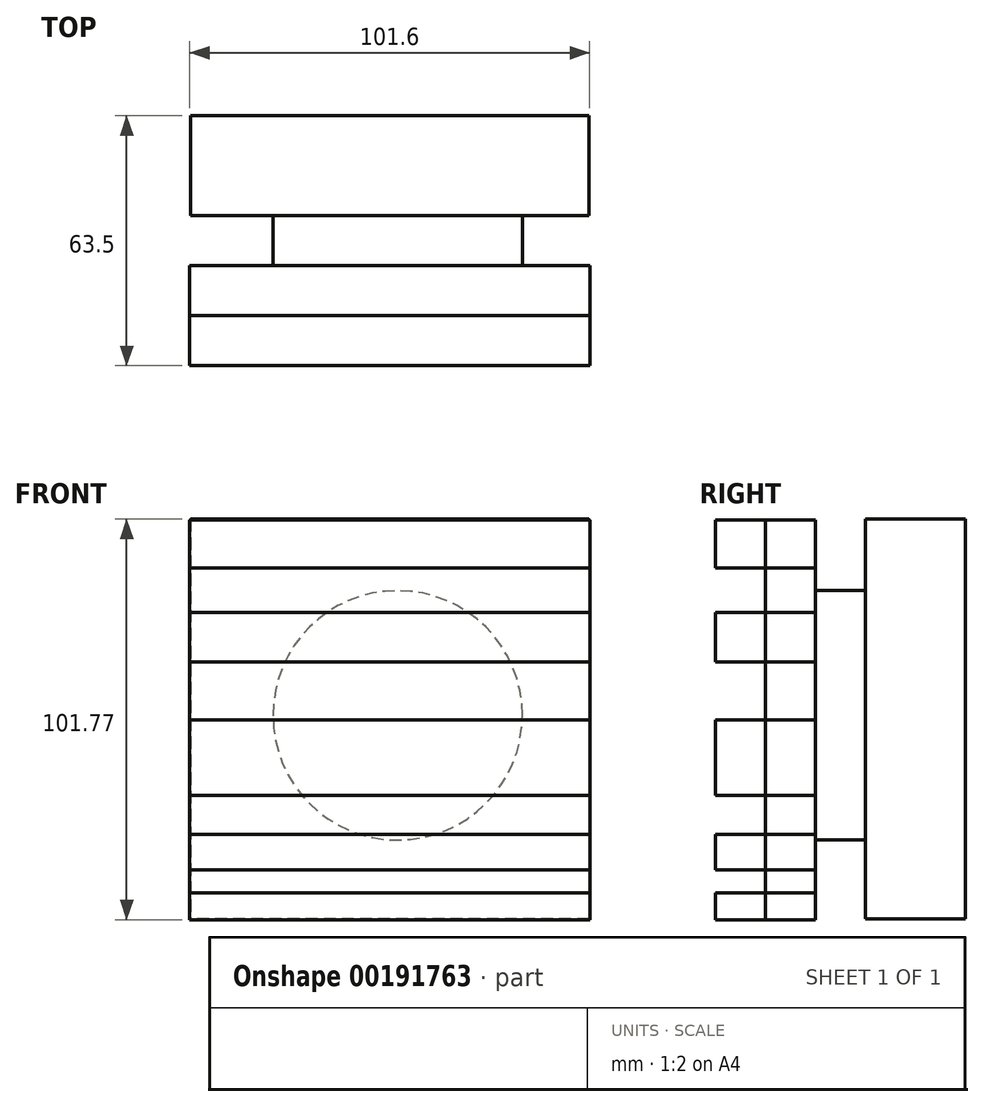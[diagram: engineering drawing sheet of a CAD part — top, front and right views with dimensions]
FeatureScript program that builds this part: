
annotation { "Feature Type Name" : "Feature", "Feature Type Description" : "" }
export const myFeature = defineFeature(function(context is Context, id is Id, definition is map)
    precondition{}
    {
        {
            var Q0;
            Q0=qCreatedBy(makeId("Front.planeOp"),FACE);
            var sketch = newSketch(context, id + "F0", { "sketchPlane" : qUnion([Q0])});
            skLineSegment(sketch, "E0.bottom", {"start": v(-49.9, 60.49) * mm, "end": v(51.7, 60.49) * mm});
            skLineSegment(sketch, "E0.top", {"start": v(-49.9, -41.11) * mm, "end": v(51.7, -41.11) * mm});
            skLineSegment(sketch, "E0.left", {"start": v(-49.9, 60.49) * mm, "end": v(-49.9, -41.11) * mm});
            skLineSegment(sketch, "E0.right", {"start": v(51.7, 60.49) * mm, "end": v(51.7, -41.11) * mm});
            skLineSegment(sketch, "E1.bottom", {"start": v(-49.9, 48.22) * mm, "end": v(51.7, 48.22) * mm});
            skLineSegment(sketch, "E1.top", {"start": v(-49.9, 36.96) * mm, "end": v(51.7, 36.96) * mm});
            skLineSegment(sketch, "E1.left", {"start": v(-49.9, 48.22) * mm, "end": v(-49.9, 36.96) * mm});
            skLineSegment(sketch, "E1.right", {"start": v(51.7, 48.22) * mm, "end": v(51.7, 36.96) * mm});
            skLineSegment(sketch, "E2.bottom", {"start": v(-49.9, 24.34) * mm, "end": v(51.7, 24.34) * mm});
            skLineSegment(sketch, "E2.top", {"start": v(-49.9, 9.69) * mm, "end": v(51.7, 9.69) * mm});
            skLineSegment(sketch, "E2.left", {"start": v(-49.9, 24.34) * mm, "end": v(-49.9, 9.69) * mm});
            skLineSegment(sketch, "E2.right", {"start": v(51.7, 24.34) * mm, "end": v(51.7, 9.69) * mm});
            skLineSegment(sketch, "E3.bottom", {"start": v(-49.9, -9.46) * mm, "end": v(51.7, -9.46) * mm});
            skLineSegment(sketch, "E3.top", {"start": v(-49.9, -19.38) * mm, "end": v(51.7, -19.38) * mm});
            skLineSegment(sketch, "E3.left", {"start": v(-49.9, -9.46) * mm, "end": v(-49.9, -19.38) * mm});
            skLineSegment(sketch, "E3.right", {"start": v(51.7, -9.46) * mm, "end": v(51.7, -19.38) * mm});
            skLineSegment(sketch, "E4.bottom", {"start": v(-49.9, -28.4) * mm, "end": v(51.7, -28.4) * mm});
            skLineSegment(sketch, "E4.top", {"start": v(-49.9, -34.25) * mm, "end": v(51.7, -34.25) * mm});
            skLineSegment(sketch, "E4.left", {"start": v(-49.9, -28.4) * mm, "end": v(-49.9, -34.25) * mm});
            skLineSegment(sketch, "E4.right", {"start": v(51.7, -28.4) * mm, "end": v(51.7, -34.25) * mm});
            skSolve(sketch);
        }
        {
            var Q0;
            {var subQ0=sQuery(id+"F0.wireOp",EDGE,"E0.bottom");Q0=makeQuery(id+"F0.imprint","IMPRINT",FACE,{"disambiguationData":[TD([[makeQuery(id+"F0.imprint","IMPRINT",EDGE,{"derivedFrom":subQ0}),-1.0]])]});}
            var Q1;
            {var subQ0=sQuery(id+"F0.wireOp",EDGE,"E0.top");Q1=makeQuery(id+"F0.imprint","IMPRINT",FACE,{"disambiguationData":[TD([[makeQuery(id+"F0.imprint","IMPRINT",EDGE,{"derivedFrom":subQ0}),1.0]])]});}
            var Q2;
            {var subQ0=sQuery(id+"F0.wireOp",EDGE,"E1.top");Q2=makeQuery(id+"F0.imprint","IMPRINT",FACE,{"disambiguationData":[TD([[makeQuery(id+"F0.imprint","IMPRINT",EDGE,{"derivedFrom":subQ0}),-1.0]])]});}
            var Q3;
            {var subQ0=sQuery(id+"F0.wireOp",EDGE,"E2.top");Q3=makeQuery(id+"F0.imprint","IMPRINT",FACE,{"disambiguationData":[TD([[makeQuery(id+"F0.imprint","IMPRINT",EDGE,{"derivedFrom":subQ0}),-1.0]])]});}
            var Q4;
            {var subQ0=sQuery(id+"F0.wireOp",EDGE,"E3.top");Q4=makeQuery(id+"F0.imprint","IMPRINT",FACE,{"disambiguationData":[TD([[makeQuery(id+"F0.imprint","IMPRINT",EDGE,{"derivedFrom":subQ0}),-1.0]])]});}
            extrude(context, id + "F1", {"entities" : qUnion([Q0, Q1, Q2, Q3, Q4]), "depth" : 12.7 * mm});
        }
        {
            var Q0;
            Q0 = qSketchRegion(id + "F0", true);
            var Q1;
            Q1=makeQuery(id+"F1.opExtrude","CAP_FACE",FACE,{"disambiguationData":[OSD([sQuery(id+"F0.wireOp",EDGE,"E0.bottom"),sQuery(id+"F0.wireOp",EDGE,"E0.left"),sQuery(id+"F0.wireOp",EDGE,"E0.right"),sQuery(id+"F0.wireOp",EDGE,"E1.bottom")])],"isStart":false});
            var Q2;
            Q2=makeQuery(id+"F1.opExtrude","CAP_FACE",FACE,{"disambiguationData":[OSD([sQuery(id+"F0.wireOp",EDGE,"E0.left"),sQuery(id+"F0.wireOp",EDGE,"E0.right"),sQuery(id+"F0.wireOp",EDGE,"E1.top"),sQuery(id+"F0.wireOp",EDGE,"E2.bottom")])],"isStart":false});
            var Q3;
            Q3=makeQuery(id+"F1.opExtrude","CAP_FACE",FACE,{"disambiguationData":[OSD([sQuery(id+"F0.wireOp",EDGE,"E0.left"),sQuery(id+"F0.wireOp",EDGE,"E0.right"),sQuery(id+"F0.wireOp",EDGE,"E2.top"),sQuery(id+"F0.wireOp",EDGE,"E3.bottom")])],"isStart":false});
            var Q4;
            Q4=makeQuery(id+"F1.opExtrude","CAP_FACE",FACE,{"disambiguationData":[OSD([sQuery(id+"F0.wireOp",EDGE,"E0.left"),sQuery(id+"F0.wireOp",EDGE,"E0.right"),sQuery(id+"F0.wireOp",EDGE,"E3.top"),sQuery(id+"F0.wireOp",EDGE,"E4.bottom")])],"isStart":false});
            var Q5;
            Q5=makeQuery(id+"F1.opExtrude","CAP_FACE",FACE,{"disambiguationData":[OSD([sQuery(id+"F0.wireOp",EDGE,"E0.top"),sQuery(id+"F0.wireOp",EDGE,"E0.left"),sQuery(id+"F0.wireOp",EDGE,"E0.right"),sQuery(id+"F0.wireOp",EDGE,"E4.top")])],"isStart":false});
            extrude(context, id + "F2", {"entities" : qUnion([Q0, Q1, Q2, Q3, Q4, Q5]), "depth" : 12.7 * mm});
        }
        {
            var Q0;
            Q0=makeQuery(id+"F1.opExtrude","CAP_FACE",FACE,{"disambiguationData":[OSD([sQuery(id+"F0.wireOp",EDGE,"E0.left"),sQuery(id+"F0.wireOp",EDGE,"E0.right"),sQuery(id+"F0.wireOp",EDGE,"E1.top"),sQuery(id+"F0.wireOp",EDGE,"E2.bottom")])],"isStart":true});
            var sketch = newSketch(context, id + "F3", { "sketchPlane" : qUnion([Q0])});
            skCircle(sketch, "E5", {"center": v(-2.91, 10.82) * mm, "radius": 31.68 * mm});
            skSolve(sketch);
        }
        {
            var Q0;
            Q0 = qSketchRegion(id + "F3", true);
            extrude(context, id + "F4", {"entities" : qUnion([Q0]), "depth" : 12.7 * mm});
        }
        {
            var Q0;
            Q0=makeQuery(id+"F4.opExtrude","CAP_FACE",FACE,{"disambiguationData":[OSD([sQuery(id+"F3.wireOp",EDGE,"E5")])],"isStart":false});
            var sketch = newSketch(context, id + "F5", { "sketchPlane" : qUnion([Q0])});
            skLineSegment(sketch, "E6.bottom", {"start": v(-51.55, 60.66) * mm, "end": v(49.75, 60.66) * mm});
            skLineSegment(sketch, "E6.top", {"start": v(-51.55, -40.9) * mm, "end": v(49.75, -40.9) * mm});
            skLineSegment(sketch, "E6.left", {"start": v(-51.55, 60.66) * mm, "end": v(-51.55, -40.9) * mm});
            skLineSegment(sketch, "E6.right", {"start": v(49.75, 60.66) * mm, "end": v(49.75, -40.9) * mm});
            skSolve(sketch);
        }
        {
            var Q0;
            Q0 = qSketchRegion(id + "F5", true);
            extrude(context, id + "F6", {"entities" : qUnion([Q0]), "operationType" : NewBodyOperationType.ADD, "depth" : 25.4 * mm});
        }
    });
